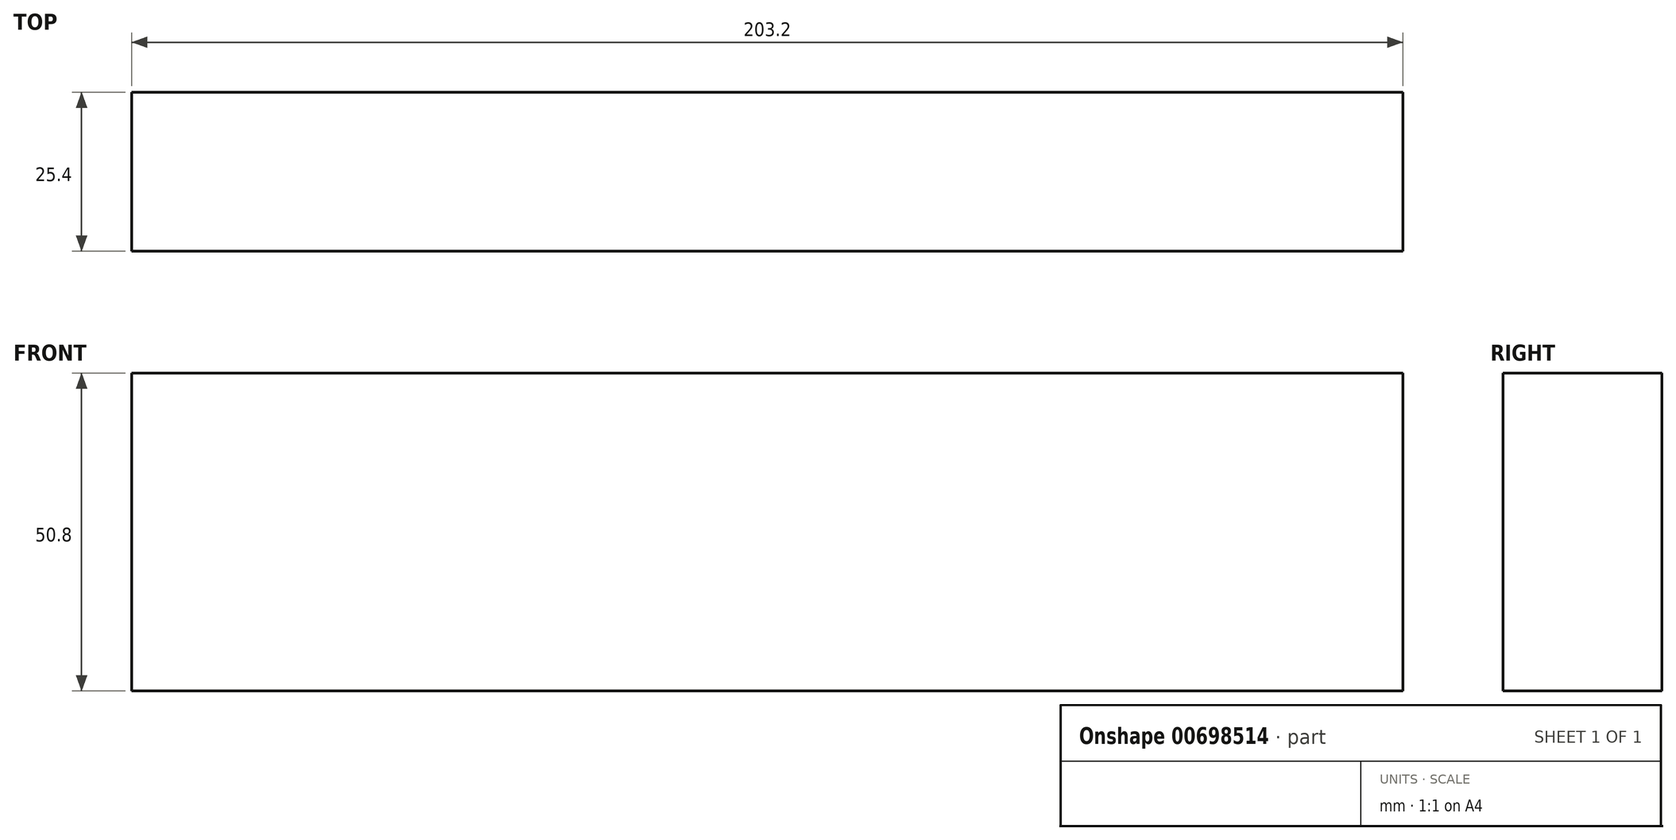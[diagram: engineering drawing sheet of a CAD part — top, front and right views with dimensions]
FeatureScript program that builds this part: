
annotation { "Feature Type Name" : "Feature", "Feature Type Description" : "" }
export const myFeature = defineFeature(function(context is Context, id is Id, definition is map)
    precondition{}
    {
        {
            var Q0;
            Q0=qCreatedBy(makeId("Front.planeOp"),FACE);
            var sketch = newSketch(context, id + "F0", { "sketchPlane" : qUnion([Q0])});
            skLineSegment(sketch, "E0.bottom", {"start": v(-206.86, -32.57) * mm, "end": v(-3.66, -32.57) * mm});
            skLineSegment(sketch, "E0.top", {"start": v(-206.86, -83.37) * mm, "end": v(-3.66, -83.37) * mm});
            skLineSegment(sketch, "E0.left", {"start": v(-206.86, -32.57) * mm, "end": v(-206.86, -83.37) * mm});
            skLineSegment(sketch, "E0.right", {"start": v(-3.66, -32.57) * mm, "end": v(-3.66, -83.37) * mm});
            skSolve(sketch);
        }
        {
            var Q0;
            Q0 = qSketchRegion(id + "F0", true);
            extrude(context, id + "F1", {"entities" : qUnion([Q0]), "depth" : 25.4 * mm, "offsetDistance" : 25.4 * mm});
        }
    });
